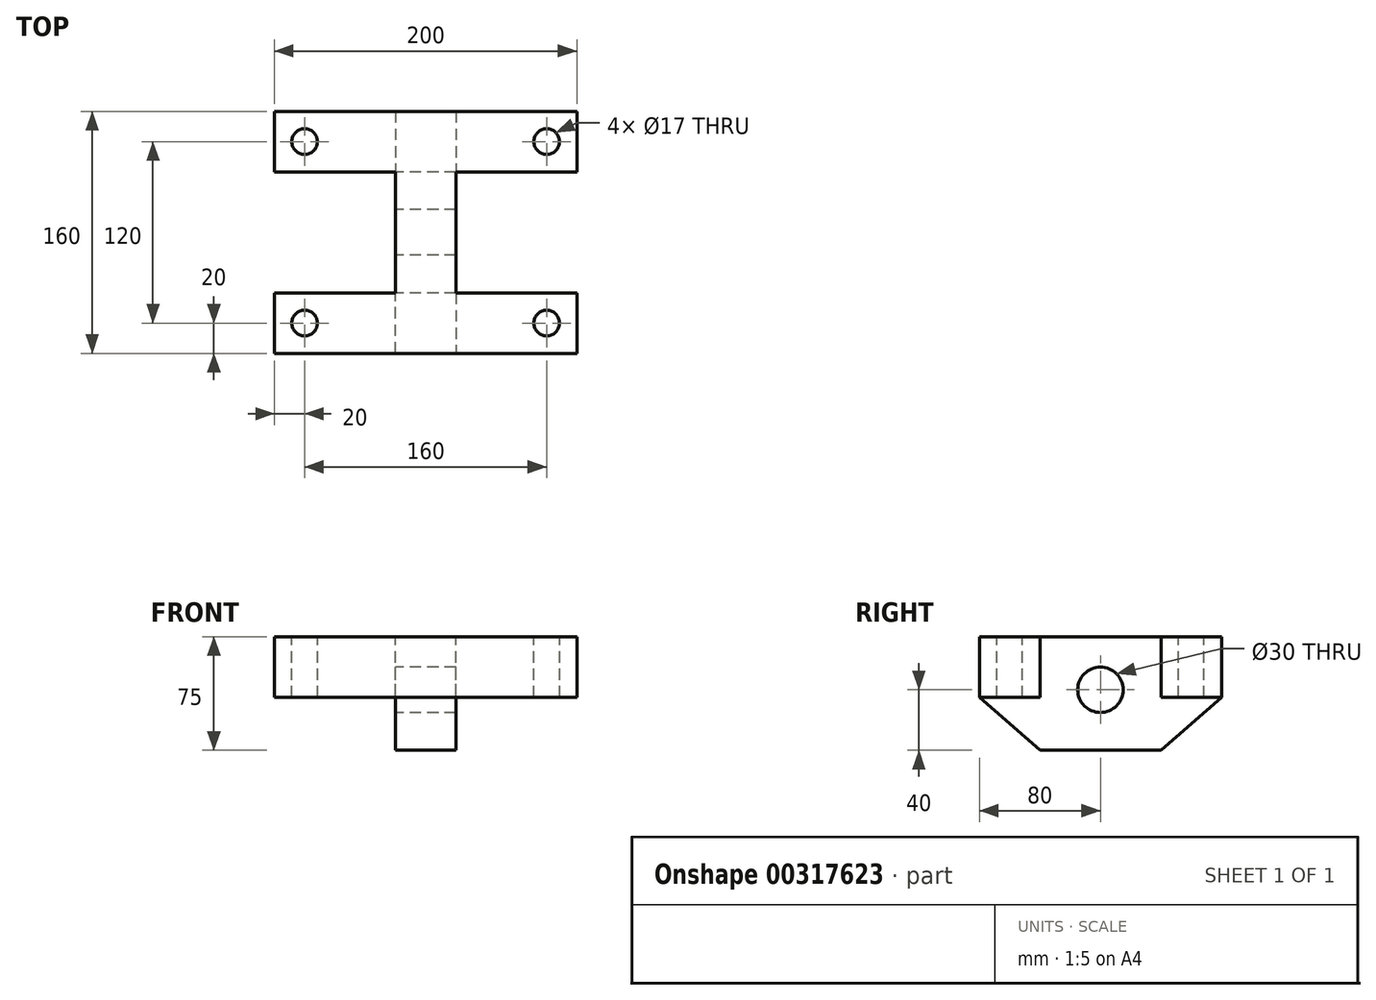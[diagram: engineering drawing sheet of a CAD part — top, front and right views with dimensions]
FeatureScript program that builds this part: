
annotation { "Feature Type Name" : "Feature", "Feature Type Description" : "" }
export const myFeature = defineFeature(function(context is Context, id is Id, definition is map)
    precondition{}
    {
        {
            var Q0;
            Q0=qCreatedBy(makeId("Right.planeOp"),FACE);
            var sketch = newSketch(context, id + "F0", { "sketchPlane" : qUnion([Q0])});
            skCircle(sketch, "E0", {"center": v(0, 0) * mm, "radius": 15 * mm});
            skLineSegment(sketch, "E1", {"start": v(-40, -40) * mm, "end": v(40, -40) * mm});
            skLineSegment(sketch, "E2", {"start": v(80, 35) * mm, "end": v(-80, 35) * mm});
            skLineSegment(sketch, "E3", {"start": v(-80, -5) * mm, "end": v(-80, 35) * mm});
            skLineSegment(sketch, "E4", {"start": v(80, -5) * mm, "end": v(80, 35) * mm});
            skLineSegment(sketch, "E5", {"start": v(-80, -5) * mm, "end": v(-40, -40) * mm});
            skLineSegment(sketch, "E6", {"start": v(40, -40) * mm, "end": v(80, -5) * mm});
            skSolve(sketch);
        }
        {
            var Q0;
            Q0 = qSketchRegion(id + "F0", true);
            extrude(context, id + "F1", {"entities" : qUnion([Q0]), "endBound" : BoundingType.SYMMETRIC, "depth" : 40 * mm});
        }
        {
            var Q0;
            Q0=qCreatedBy(makeId("Right.planeOp"),FACE);
            var sketch = newSketch(context, id + "F2", { "sketchPlane" : qUnion([Q0])});
            skLineSegment(sketch, "E7.bottom", {"start": v(-80, 35) * mm, "end": v(-40, 35) * mm});
            skLineSegment(sketch, "E7.top", {"start": v(-80, -5) * mm, "end": v(-40, -5) * mm});
            skLineSegment(sketch, "E7.left", {"start": v(-80, 35) * mm, "end": v(-80, -5) * mm});
            skLineSegment(sketch, "E7.right", {"start": v(-40, 35) * mm, "end": v(-40, -5) * mm});
            skLineSegment(sketch, "E8.bottom", {"start": v(40, 35) * mm, "end": v(80, 35) * mm});
            skLineSegment(sketch, "E8.top", {"start": v(40, -5) * mm, "end": v(80, -5) * mm});
            skLineSegment(sketch, "E8.left", {"start": v(40, 35) * mm, "end": v(40, -5) * mm});
            skLineSegment(sketch, "E8.right", {"start": v(80, 35) * mm, "end": v(80, -5) * mm});
            skSolve(sketch);
        }
        {
            var Q0;
            Q0 = qSketchRegion(id + "F2", true);
            extrude(context, id + "F3", {"entities" : qUnion([Q0]), "operationType" : NewBodyOperationType.ADD, "endBound" : BoundingType.SYMMETRIC, "depth" : 200 * mm});
        }
        {
            var Q0;
            Q0=makeQuery(id+"F3.boolean.opBoolean","MERGE",FACE,{"derivedFrom":[makeQuery(id+"F1.opExtrude","SWEPT_FACE",FACE,{"disambiguationData":[OSD([sQuery(id+"F0.wireOp",EDGE,"E2")])]}),makeQuery(id+"F3.opExtrude","SWEPT_FACE",FACE,{"disambiguationData":[OSD([sQuery(id+"F2.wireOp",EDGE,"E7.bottom")])]}),makeQuery(id+"F3.opExtrude","SWEPT_FACE",FACE,{"disambiguationData":[OSD([sQuery(id+"F2.wireOp",EDGE,"E8.bottom")])]})]});
            var sketch = newSketch(context, id + "F4", { "sketchPlane" : qUnion([Q0])});
            skPoint(sketch, "E9", {"position": v(-80, -60) * mm});
            skPoint(sketch, "E10", {"position": v(80, -60) * mm});
            skPoint(sketch, "E11", {"position": v(80, 60) * mm});
            skPoint(sketch, "E12", {"position": v(-80, 60) * mm});
            skSolve(sketch);
        }
        {
            var Q0;
            Q0=sQuery(id+"F4.wireOp",VERTEX,"E12");
            var Q1;
            Q1=sQuery(id+"F4.wireOp",VERTEX,"E11");
            var Q2;
            Q2=sQuery(id+"F4.wireOp",VERTEX,"E10");
            var Q3;
            Q3=sQuery(id+"F4.wireOp",VERTEX,"E9");
            var Q4;
            Q4=makeQuery(id+"F1.opExtrude","SWEPT_BODY",BODY,{"disambiguationData":[OSD([sQuery(id+"F0.wireOp",EDGE,"E0"),sQuery(id+"F0.wireOp",EDGE,"E1"),sQuery(id+"F0.wireOp",EDGE,"E2"),sQuery(id+"F0.wireOp",EDGE,"E3"),sQuery(id+"F0.wireOp",EDGE,"E4"),sQuery(id+"F0.wireOp",EDGE,"E5"),sQuery(id+"F0.wireOp",EDGE,"E6")])]});
            hole(context, id + "F5", {"style" : HoleStyle.SIMPLE, "endStyle" : HoleEndStyle.THROUGH, "holeDiameter" : 17 * mm, "tappedDepth" : 12 * mm, "tapClearance" : 3, "locations" : qUnion([Q0, Q1, Q2, Q3]), "scope" : qUnion([Q4])});
        }
    });
